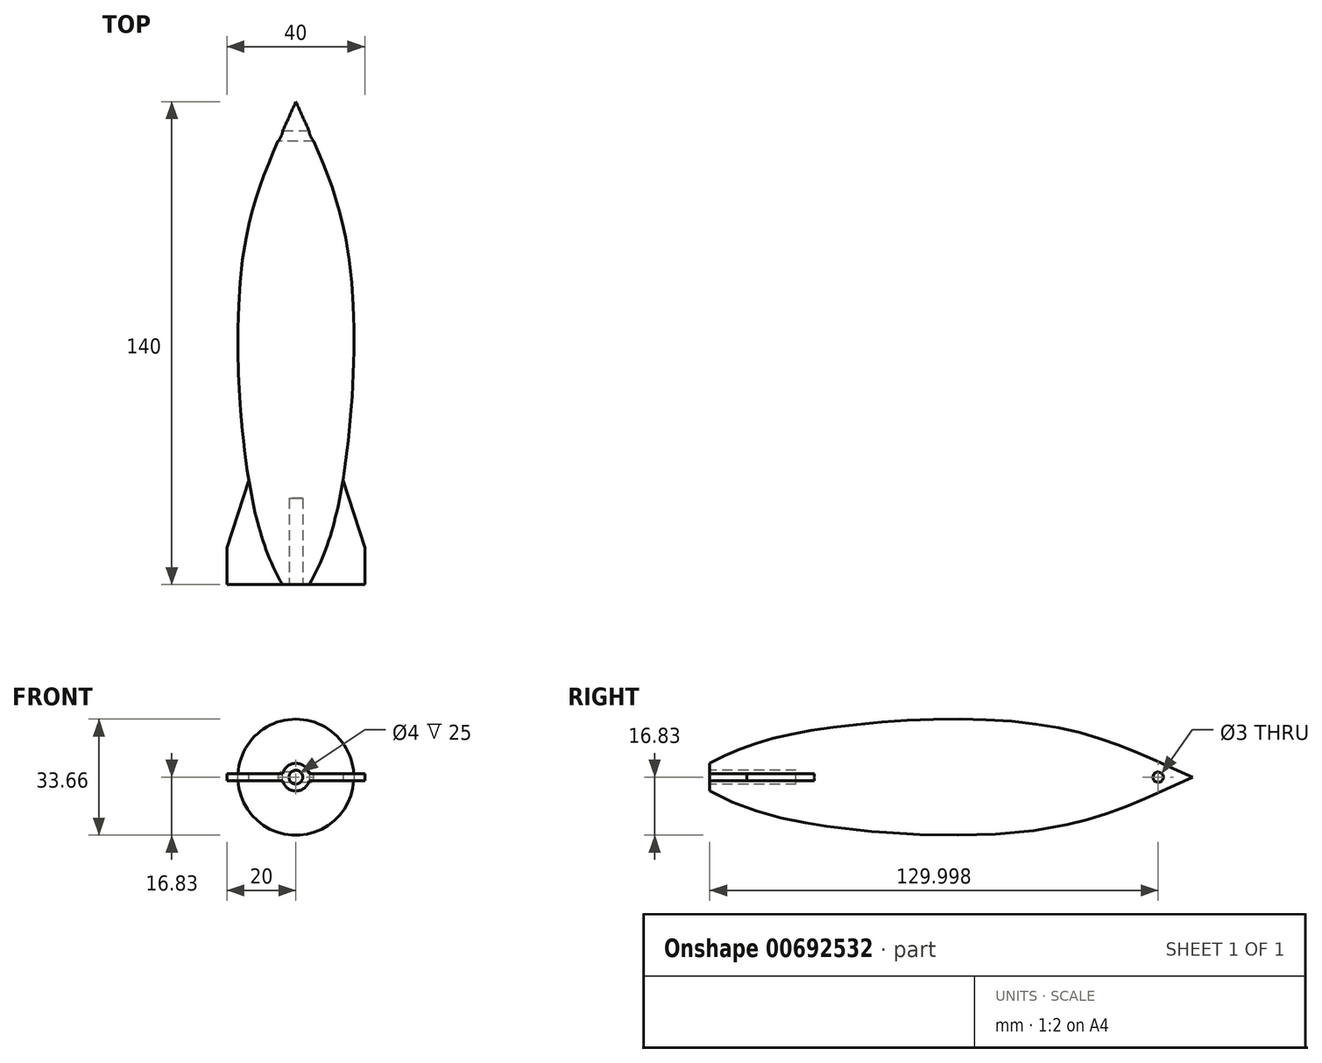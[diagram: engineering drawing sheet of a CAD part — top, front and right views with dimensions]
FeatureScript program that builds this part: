
annotation { "Feature Type Name" : "Feature", "Feature Type Description" : "" }
export const myFeature = defineFeature(function(context is Context, id is Id, definition is map)
    precondition{}
    {
        {
            var Q0;
            Q0=qCreatedBy(makeId("Right.planeOp"),FACE);
            var sketch = newSketch(context, id + "F0", { "sketchPlane" : qUnion([Q0])});
            skLineSegment(sketch, "E0", {"start": v(-90.5, 0) * mm, "end": v(49.5, 0) * mm});
            skLineSegment(sketch, "E1", {"start": v(-90.5, 0) * mm, "end": v(-90.5, 4) * mm});
            skFitSpline(sketch, "E2", {"points": [v(-90.5, 4) * mm, v(-57.7, 14.05) * mm, v(8.06, 14.8) * mm, v(49.5, 0) * mm], "startDerivative": vector(96.77, 54.85) * mm, "endDerivative": vector(126.52, -56.53) * mm});
            skCircle(sketch, "E3", {"center": v(39.5, 0) * mm, "radius": 1.5 * mm});
            skSolve(sketch);
        }
        {
            var Q0;
            Q0 = qSketchRegion(id + "F0", true);
            var Q1;
            Q1=sQuery(id+"F0.wireOp",EDGE,"E0");
            revolve(context, id + "F1", {"entities" : qUnion([Q0]), "axis" : qUnion([Q1]), "revolveType" : RevolveType.FULL});
        }
        {
            var Q0;
            Q0=makeQuery(id+"F1.opRevolve","SWEPT_FACE",FACE,{"disambiguationData":[OSD([sQuery(id+"F0.wireOp",EDGE,"E1")])]});
            var sketch = newSketch(context, id + "F2", { "sketchPlane" : qUnion([Q0])});
            skLineSegment(sketch, "E4", {"start": v(0, 0) * mm, "end": v(0, 1) * mm});
            skLineSegment(sketch, "E5", {"start": v(0, 0) * mm, "end": v(0, -1) * mm});
            skLineSegment(sketch, "E6.bottom", {"start": v(0, 1) * mm, "end": v(-20, 1) * mm});
            skLineSegment(sketch, "E6.top", {"start": v(0, -1) * mm, "end": v(-20, -1) * mm});
            skLineSegment(sketch, "E6.left", {"start": v(0, 1) * mm, "end": v(0, -1) * mm});
            skLineSegment(sketch, "E6.right", {"start": v(-20, 1) * mm, "end": v(-20, -1) * mm});
            skLineSegment(sketch, "E7.bottom", {"start": v(0, 1) * mm, "end": v(20, 1) * mm});
            skLineSegment(sketch, "E7.top", {"start": v(0, -1) * mm, "end": v(20, -1) * mm});
            skLineSegment(sketch, "E7.right", {"start": v(20, 1) * mm, "end": v(20, -1) * mm});
            skSolve(sketch);
        }
        {
            var Q0;
            Q0 = qSketchRegion(id + "F2", true);
            extrude(context, id + "F3", {"entities" : qUnion([Q0]), "operationType" : NewBodyOperationType.ADD, "oppositeDirection" : true, "depth" : 30.7 * mm, "offsetDistance" : 25 * mm});
        }
        {
            var Q0;
            Q0=makeQuery(id+"F3.opExtrude","CAP_EDGE",EDGE,{"disambiguationData":[OSD([sQuery(id+"F2.wireOp",EDGE,"E7.right")])],"isStart":false});
            chamfer(context, id + "F4", {"entities" : qUnion([Q0]), "chamferType" : ChamferType.TWO_OFFSETS, "width1" : 6.5 * mm, "oppositeDirection" : false, "width2" : 20 * mm, "tangentPropagation" : true});
        }
        {
            var Q0;
            Q0=makeQuery(id+"F3.opExtrude","CAP_EDGE",EDGE,{"disambiguationData":[OSD([sQuery(id+"F2.wireOp",EDGE,"E6.right")])],"isStart":false});
            chamfer(context, id + "F5", {"entities" : qUnion([Q0]), "chamferType" : ChamferType.TWO_OFFSETS, "width1" : 6.5 * mm, "oppositeDirection" : true, "width2" : 20 * mm, "tangentPropagation" : true});
        }
        {
            var Q0;
            Q0=makeQuery(id+"F3.boolean.opBoolean","MERGE",FACE,{"derivedFrom":[makeQuery(id+"F1.opRevolve","SWEPT_FACE",FACE,{"disambiguationData":[OSD([sQuery(id+"F0.wireOp",EDGE,"E1")])]}),makeQuery(id+"F3.opExtrude","CAP_FACE",FACE,{"disambiguationData":[OSD([sQuery(id+"F2.wireOp",EDGE,"E6.bottom"),sQuery(id+"F2.wireOp",EDGE,"E6.top"),sQuery(id+"F2.wireOp",EDGE,"E6.right"),sQuery(id+"F2.wireOp",EDGE,"E7.bottom"),sQuery(id+"F2.wireOp",EDGE,"E7.top"),sQuery(id+"F2.wireOp",EDGE,"E7.right")])],"isStart":true})]});
            var sketch = newSketch(context, id + "F6", { "sketchPlane" : qUnion([Q0])});
            skCircle(sketch, "E8", {"center": v(0, 0) * mm, "radius": 2 * mm});
            skSolve(sketch);
        }
        {
            var Q0;
            Q0 = qSketchRegion(id + "F6", true);
            extrude(context, id + "F7", {"entities" : qUnion([Q0]), "operationType" : NewBodyOperationType.REMOVE, "oppositeDirection" : true, "depth" : 25 * mm, "offsetDistance" : 25 * mm});
        }
        {
            var Q0;
            Q0=sQuery(id+"F0.wireOp",VERTEX,"E3.center");
            var Q1;
            Q1=makeQuery(id+"F1.opRevolve","SWEPT_BODY",BODY,{"disambiguationData":[OSD([sQuery(id+"F0.wireOp",EDGE,"E0"),sQuery(id+"F0.wireOp",EDGE,"E1"),sQuery(id+"F0.wireOp",EDGE,"E2"),sQuery(id+"F0.wireOp",EDGE,"E3")])]});
            hole(context, id + "F8", {"style" : HoleStyle.SIMPLE, "endStyle" : HoleEndStyle.THROUGH, "oppositeDirection" : true, "holeDiameter" : 3 * mm, "majorDiameter" : 5 * mm, "isTappedThrough" : true, "tappedDepth" : 12 * mm, "tapClearance" : 3, "locations" : qUnion([Q0]), "scope" : qUnion([Q1])});
        }
        {
            var Q0;
            Q0=sQuery(id+"F0.wireOp",VERTEX,"E3.center");
            var Q1;
            Q1=makeQuery(id+"F1.opRevolve","SWEPT_BODY",BODY,{"disambiguationData":[OSD([sQuery(id+"F0.wireOp",EDGE,"E0"),sQuery(id+"F0.wireOp",EDGE,"E1"),sQuery(id+"F0.wireOp",EDGE,"E2"),sQuery(id+"F0.wireOp",EDGE,"E3")])]});
            hole(context, id + "F9", {"style" : HoleStyle.SIMPLE, "endStyle" : HoleEndStyle.THROUGH, "holeDiameter" : 3 * mm, "majorDiameter" : 5 * mm, "isTappedThrough" : true, "tappedDepth" : 12 * mm, "tapClearance" : 3, "locations" : qUnion([Q0]), "scope" : qUnion([Q1])});
        }
    });
